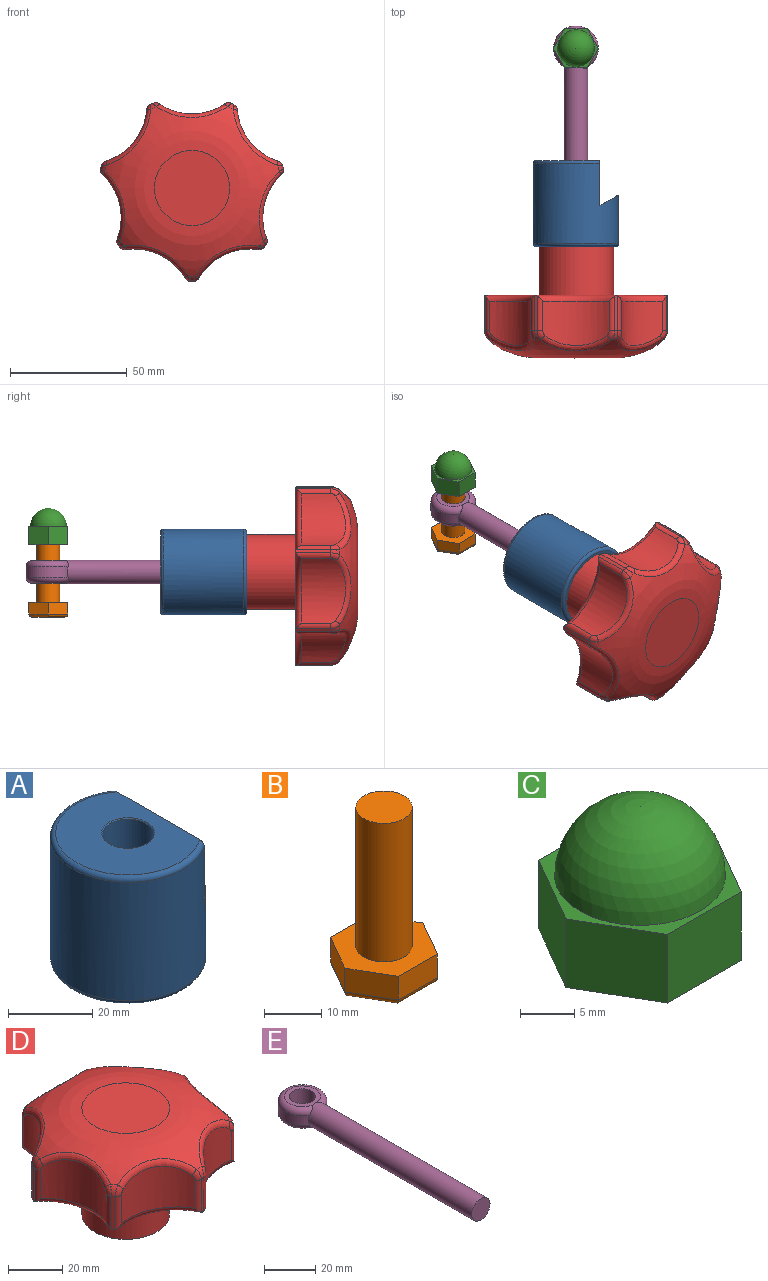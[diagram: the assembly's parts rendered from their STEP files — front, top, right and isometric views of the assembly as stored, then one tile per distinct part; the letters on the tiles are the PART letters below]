
ASSEMBLY  parts=5 mates=5
PART A: 11 faces, bbox 39.9x39.9x36.9 mm
  f0: cylinder r=18.41mm len=36.83mm, axis (0,0,-1), area 3298.3mm2, adj f1,f2,f4,f8,f9
  f1: torus R=17.14mm, axis (0,0,1), area 221.1mm2, adj f0,f6,f9
  f2: plane 30.76x8.03mm, normal (-0.5,0,0.87), area 206mm2, adj f0,f8,f9
  f3: plane 34.29x27.27mm, normal (0,0,1), area 664.2mm2, adj f4,f7,f8
  f4: torus R=17.14mm, axis (0,0,1), area 155.5mm2, adj f0,f3,f8
  f5: cylinder r=6.01mm len=36.5mm, axis (0,0,-1), area 1379.1mm2, adj f7,f10
  f6: plane 34.29x34.29mm, normal (0,0,-1), area 805mm2, adj f1,f10
  f7: cone r=6.01mm half-angle=45deg, axis (0,0,1), area 13.9mm2, adj f3,f5
  f8: plane 30.76x19.43mm, normal (1,0,0), area 596.8mm2, adj f0,f2,f3,f4
  f9: plane 21.58x6.1mm, normal (1,0,0), area 130.6mm2, adj f0,f1,f2
  f10: torus R=6.14mm, axis (0,0,1), area 7.6mm2, adj f5,f6
PART B: 16 faces, bbox 19.4x16.8x36 mm
  f0: plane 8.38x5.08mm, normal (0.87,-0.5,0), area 49.2mm2, adj f1,f5,f6,f10
  f1: plane 8.38x5.08mm, normal (0.87,0.5,0), area 49.2mm2, adj f0,f2,f6,f8
  f2: plane 9.68x5.08mm, normal (0,1,0), area 49.2mm2, adj f1,f3,f6,f9
  f3: plane 8.38x5.08mm, normal (-0.87,0.5,0), area 49.2mm2, adj f2,f4,f6,f11
  f4: plane 8.38x5.08mm, normal (-0.87,-0.5,0), area 49.2mm2, adj f3,f5,f6,f13
  f5: plane 9.68x5.08mm, normal (0,-1,0), area 49.2mm2, adj f0,f4,f6,f12
  f6: plane 19.36x16.76mm, normal (0,0,1), area 166.7mm2, adj f0,f1,f2,f3,f4,f5,f14
  f7: plane 16.42x14.22mm, normal (0,0,-1), area 175.2mm2, adj f8,f9,f10,f11,f12,f13
  f8: cylinder r=1.27mm len=9.02mm, axis (-0.5,0.87,0), area 18.2mm2, adj f1,f7,f9,f10
  f9: cylinder r=1.27mm len=9.68mm, axis (-1,0,0), area 18.2mm2, adj f2,f7,f8,f11
  f10: cylinder r=1.27mm len=9.02mm, axis (0.5,0.87,0), area 18.2mm2, adj f0,f7,f8,f12
  f11: cylinder r=1.27mm len=9.02mm, axis (-0.5,-0.87,0), area 18.2mm2, adj f3,f7,f9,f13
  f12: cylinder r=1.27mm len=9.68mm, axis (1,0,0), area 18.2mm2, adj f5,f7,f10,f13
  f13: cylinder r=1.27mm len=9.02mm, axis (0.5,-0.87,0), area 18.2mm2, adj f4,f7,f11,f12
  f14: cylinder r=4.94mm len=29.69mm, axis (0,0,-1), area 921.7mm2, adj f6,f15
  f15: plane 9.88x9.88mm, normal (0,0,1), area 76.7mm2, adj f14
PART C: 11 faces, bbox 19.4x16.8x15.6 mm
  f0: plane 8.38x7.75mm, normal (0.87,-0.5,0), area 75mm2, adj f1,f5,f6,f7
  f1: plane 8.38x7.75mm, normal (0.87,0.5,0), area 75mm2, adj f0,f2,f6,f7
  f2: plane 9.68x7.75mm, normal (0,1,0), area 75mm2, adj f1,f3,f6,f7
  f3: plane 8.38x7.75mm, normal (-0.87,0.5,0), area 75mm2, adj f2,f4,f6,f7
  f4: plane 8.38x7.75mm, normal (-0.87,-0.5,0), area 75mm2, adj f3,f5,f6,f7
  f5: plane 9.68x7.75mm, normal (0,-1,0), area 75mm2, adj f0,f4,f6,f7
  f6: plane 19.36x16.76mm, normal (0,0,1), area 48mm2, adj f0,f1,f2,f3,f4,f5,f8
  f7: plane 19.36x16.76mm, normal (0,0,-1), area 185.8mm2, adj f0,f1,f2,f3,f4,f5,f9
  f8: sphere r=7.89mm, area 390.8mm2, adj f6
  f9: cylinder r=4.28mm len=12.7mm, axis (0,0,-1), area 341.5mm2, adj f7,f10
  f10: plane 8.56x8.56mm, normal (0,0,-1), area 57.5mm2, adj f9
PART D: 70 faces, bbox 80.3x78.8x47.7 mm
  f0: torus R=16.09mm, axis (0,0,1), area 2755.1mm2, adj f3,f4,f6,f9,f10,f13,f14,f20
  f1: cylinder r=39.94mm len=15.03mm, axis (0,0,1), area 21.4mm2, adj f3,f56,f64,f68,f69
  f2: cylinder r=39.94mm len=15.03mm, axis (0,0,1), area 21.3mm2, adj f4,f61,f65,f66,f68
  f3: torus R=34.86mm, axis (0,0,-1), area 9.4mm2, adj f0,f1,f46,f67
  f4: torus R=34.86mm, axis (0,0,-1), area 9.4mm2, adj f0,f2,f55,f62
  f5: cylinder r=39.94mm len=15.03mm, axis (0,0,1), area 21.4mm2, adj f6,f48,f57,f58,f64
  f6: torus R=34.86mm, axis (0,0,-1), area 9.4mm2, adj f0,f5,f37,f47
  f7: cylinder r=39.94mm len=15.03mm, axis (0,0,1), area 21.4mm2, adj f10,f40,f41,f50,f51
  f8: cylinder r=39.94mm len=15.03mm, axis (0,0,1), area 21.4mm2, adj f9,f39,f49,f50,f58
  f9: torus R=34.86mm, axis (0,0,-1), area 9.4mm2, adj f0,f8,f31,f38
  f10: torus R=34.86mm, axis (0,0,-1), area 9.4mm2, adj f0,f7,f32,f33
  f11: cylinder r=39.94mm len=15.03mm, axis (0,0,1), area 21.4mm2, adj f13,f53,f59,f60,f65
  f12: cylinder r=39.94mm len=15.03mm, axis (0,0,1), area 21.4mm2, adj f14,f42,f51,f52,f59
  f13: torus R=34.86mm, axis (0,0,-1), area 9.4mm2, adj f0,f11,f44,f54
  f14: torus R=34.86mm, axis (0,0,-1), area 9.4mm2, adj f0,f12,f34,f43
  f15: cylinder r=16.09mm len=32.18mm, axis (0,0,-1), area 2110.9mm2, adj f16,f19
  f16: plane 32.18x32.18mm, normal (0,0,-1), area 729.1mm2, adj f15,f17
  f17: cylinder r=5.18mm len=45.36mm, axis (0,0,-1), area 1476.9mm2, adj f16,f18
  f18: plane 10.36x10.36mm, normal (0,0,-1), area 84.3mm2, adj f17
  f19: plane 75.29x73.41mm, normal (0,0,-1), area 2375.1mm2, adj f15,f50,f51,f58,f59,f64,f65,f68
  f20: plane 32.18x32.18mm, normal (0,0,1), area 813.4mm2, adj f0
  f21: cylinder r=25.4mm len=28.4mm, axis (0,0,-1), area 521.8mm2, adj f45,f54,f55,f60,f61,f65
  f22: cylinder r=25.4mm len=27.69mm, axis (0,0,-1), area 521.8mm2, adj f29,f33,f34,f41,f42,f51
  f23: cylinder r=25.4mm len=25.59mm, axis (0,0,-1), area 521.8mm2, adj f30,f37,f38,f48,f49,f58
  f24: cylinder r=25.4mm len=22.2mm, axis (0,0,-1), area 521.8mm2, adj f35,f43,f44,f52,f53,f59
  f25: cylinder r=25.4mm len=25.59mm, axis (0,0,-1), area 521.8mm2, adj f28,f31,f32,f39,f40,f50
  f26: cylinder r=25.4mm len=27.69mm, axis (0,0,-1), area 521.8mm2, adj f36,f46,f47,f56,f57,f64
  f27: cylinder r=25.4mm len=22.2mm, axis (0,0,-1), area 521.8mm2, adj f62,f63,f66,f67,f68,f69
  f28: bspline ~31.13x16.06mm, area 94.8mm2, adj f0,f25,f31,f32
  f29: bspline ~33.68x11.16mm, area 94.8mm2, adj f0,f22,f33,f34
  f30: bspline ~31.12x16.06mm, area 94.8mm2, adj f0,f23,f37,f38
  f31: bspline ~5.4x2.87mm, area 9.8mm2, adj f9,f25,f28,f39
  f32: bspline ~5.4x3.69mm, area 9.8mm2, adj f10,f25,f28,f40
  f33: bspline ~5.4x3.76mm, area 9.8mm2, adj f10,f22,f29,f41
  f34: bspline ~5.4x3.34mm, area 9.8mm2, adj f14,f22,f29,f42
  f35: bspline ~27.01x21.63mm, area 94.8mm2, adj f0,f24,f43,f44
  f36: bspline ~33.68x11.16mm, area 94.8mm2, adj f0,f26,f46,f47
  f37: bspline ~5.4x3.69mm, area 9.8mm2, adj f6,f23,f30,f48
  f38: bspline ~5.4x2.87mm, area 9.8mm2, adj f9,f23,f30,f49
  f39: cylinder r=2.54mm len=14.78mm, axis (0,0,-1), area 35.6mm2, adj f8,f25,f31,f50
  f40: cylinder r=2.54mm len=14.78mm, axis (0,0,1), area 35.6mm2, adj f7,f25,f32,f50
  f41: cylinder r=2.54mm len=14.78mm, axis (0,0,-1), area 35.6mm2, adj f7,f22,f33,f51
  f42: cylinder r=2.54mm len=14.78mm, axis (0,0,1), area 35.6mm2, adj f12,f22,f34,f51
  f43: bspline ~5.4x3.01mm, area 9.8mm2, adj f14,f24,f35,f52
  f44: bspline ~5.4x3.43mm, area 9.8mm2, adj f13,f24,f35,f53
  f45: bspline ~34.55x8.36mm, area 94.8mm2, adj f0,f21,f54,f55
  f46: bspline ~5.4x3.34mm, area 9.8mm2, adj f3,f26,f36,f56
  f47: bspline ~5.4x3.76mm, area 9.8mm2, adj f6,f26,f36,f57
  f48: cylinder r=2.54mm len=14.78mm, axis (0,0,-1), area 35.6mm2, adj f5,f23,f37,f58
  f49: cylinder r=2.54mm len=14.78mm, axis (0,0,1), area 35.6mm2, adj f8,f23,f38,f58
  f50: torus R=27.94mm, axis (0,0,1), area 135.9mm2, adj f7,f8,f19,f25,f39,f40,f51,f58
  f51: torus R=27.94mm, axis (0,0,1), area 135.9mm2, adj f7,f12,f19,f22,f41,f42,f50,f59
  f52: cylinder r=2.54mm len=14.78mm, axis (0,0,-1), area 35.6mm2, adj f12,f24,f43,f59
  f53: cylinder r=2.54mm len=14.78mm, axis (0,0,1), area 35.6mm2, adj f11,f24,f44,f59
  f54: bspline ~5.4x3.64mm, area 9.8mm2, adj f13,f21,f45,f60
  f55: bspline ~5.4x3.64mm, area 9.8mm2, adj f4,f21,f45,f61
  f56: cylinder r=2.54mm len=14.78mm, axis (0,0,-1), area 35.6mm2, adj f1,f26,f46,f64
  f57: cylinder r=2.54mm len=14.78mm, axis (0,0,1), area 35.6mm2, adj f5,f26,f47,f64
  f58: torus R=27.94mm, axis (0,0,1), area 135.9mm2, adj f5,f8,f19,f23,f48,f49,f50,f64
  f59: torus R=27.94mm, axis (0,0,1), area 135.9mm2, adj f11,f12,f19,f24,f51,f52,f53,f65
  f60: cylinder r=2.54mm len=14.78mm, axis (0,0,-1), area 35.6mm2, adj f11,f21,f54,f65
  f61: cylinder r=2.54mm len=14.78mm, axis (0,0,1), area 35.6mm2, adj f2,f21,f55,f65
  f62: bspline ~5.4x3.43mm, area 9.8mm2, adj f4,f27,f63,f66
  f63: bspline ~27.01x21.63mm, area 94.8mm2, adj f0,f27,f62,f67
  f64: torus R=27.94mm, axis (0,0,1), area 135.9mm2, adj f1,f5,f19,f26,f56,f57,f58,f68
  f65: torus R=27.94mm, axis (0,0,1), area 135.9mm2, adj f2,f11,f19,f21,f59,f60,f61,f68
  f66: cylinder r=2.54mm len=14.78mm, axis (0,0,-1), area 35.6mm2, adj f2,f27,f62,f68
  f67: bspline ~5.4x3.01mm, area 9.8mm2, adj f3,f27,f63,f69
  f68: torus R=27.94mm, axis (0,0,1), area 135.9mm2, adj f1,f2,f19,f27,f64,f65,f66,f69
  f69: cylinder r=2.54mm len=14.78mm, axis (0,0,1), area 35.6mm2, adj f1,f27,f67,f68
PART E: 10 faces, bbox 20.7x108.9x10.2 mm
  f0: cylinder r=9.58mm len=19.15mm, axis (0,0,-1), area 230.6mm2, adj f1,f2,f7
  f1: torus R=7.04mm, axis (0,0,1), area 193.1mm2, adj f0,f5,f6,f7
  f2: torus R=7.04mm, axis (0,0,1), area 193.1mm2, adj f0,f4,f7,f9
  f3: cylinder r=5.08mm len=10.16mm, axis (0,0,-1), area 309.7mm2, adj f4,f5
  f4: plane 14.07x14.07mm, normal (0,0,1), area 74.4mm2, adj f2,f3
  f5: plane 14.07x14.07mm, normal (0,0,-1), area 74.4mm2, adj f1,f3
  f6: plane 3.09x0.24mm, normal (0,1,0), area 0.5mm2, adj f1,f7
  f7: cylinder r=5.08mm len=91.44mm, axis (0,1,0), area 2889.8mm2, adj f0,f1,f2,f6,f8,f9
  f8: plane 10.16x10.16mm, normal (0,-1,0), area 81.1mm2, adj f7
  f9: plane 3.09x0.24mm, normal (0,1,0), area 0.5mm2, adj f2,f7
PLACE A rot(axis=(-1,0,0),90deg) t=(126.41,9.78,16.34)mm
PLACE B t=(126.41,94.74,-2.94)mm
PLACE C t=(126.41,94.74,28.02)mm
PLACE D rot(axis=(1,0,0),90deg) t=(126.41,9.78,16.34)mm
PLACE E t=(126.41,94.74,16.34)mm
MATE fastened C.f9 <-> B.f14  axis (0,0,-1) through (126.41,94.74,28.02)mm
MATE slider A.f5 <-> E.f7  axis (0,-1,0) through (126.41,9.9,16.34)mm
MATE slider B.f14 <-> E.f3  axis (0,0,-1) through (126.41,94.74,18.26)mm
MATE slider D.f17 <-> E.f7  axis (0,1,0) through (126.41,9.78,16.34)mm
MATE fastened D.f3 <-> A.f0  axis (0,1,0) through (126.41,9.78,16.34)mm
